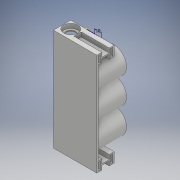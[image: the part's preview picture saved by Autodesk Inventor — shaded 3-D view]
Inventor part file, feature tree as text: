
AUTODESK INVENTOR PART (.ipt)
format: ipt  version: 2018 (Build 220112000, 112)  size: 634,368 bytes
history: native  units: mm
features: sketch x16, extrude x13, fillet x3
ambient origin geometry x8: Origin, YZ Plane, XZ Plane, XY Plane, X Axis, Y Axis, Z Axis, Center Point
bodies: Solid1 (feature_tree)
feature tree (32):
  extrude  "Extrusion1"  Depth=165.0mm
  extrude  "Extrusion2"  Depth=8.5mm
  extrude  "Extrusion3"  Depth=25.0mm TaperAngle=0.0deg
  extrude  "Extrusion4"  Depth=22.75mm
  extrude  "Extrusion5"  Depth=7.1mm
  extrude  "Extrusion6"  Depth=7.1mm TaperAngle=0.0deg
  fillet  "Fillet1"  Radius=5.0mm
  extrude  "Extrusion7"  Depth=10.0mm TaperAngle=0.0deg
  fillet  "Fillet2"  Radius=2.0mm
  extrude  "Extrusion8"  Depth=8.0mm
  extrude  "Extrusion9"  Depth=16.0mm
  fillet  "Fillet3"  Radius=8.0mm
  extrude  "Extrusion10"  Depth=6.0mm
  extrude  "Extrusion11"  Depth=3.5mm
  sketch  "Sketch12"  dims[d32=12.25mm d33=3.5mm]
  sketch  "Sketch13"  dims[d34=12.25mm d35=12.25mm]
  extrude  "Extrusion12"  Depth=3.5mm
  extrude  "Extrusion13"  Depth=12.25mm
  sketch  "Sketch16"  dims[d39=1.0mm d40=2.0mm d41=8.0mm d42=1.0mm d43=2.0mm d44=12.0mm d45=0.0mm d46=6.0mm d47=7.1mm d48=0.0mm d49=3.0mm d50=0.0mm d51=42.0mm d52=38.75mm d53=42.0mm d54=38.75mm d55=42.0mm d56=38.75mm d57=45.0mm d58=0.0mm d59=2.0mm d60=4.0mm d61=2.0mm d62=4.0mm d63=45.0mm d64=0.0mm d65=10.0mm]
  sketch  "Sketch1"  dims[d0=25.0mm d1=165.0mm]
  sketch  "Sketch2"  dims[d2=3.0mm d3=0.0mm d4=8.5mm]
  sketch  "Sketch3"  dims[d5=8.5mm d6=25.0mm d7=0.0mm]
  sketch  "Sketch4"  dims[d8=25.0mm d9=22.75mm]
  sketch  "Sketch5"  dims[d10=7.1mm d11=0.0mm d12=15.5mm]
  sketch  "Sketch6"  dims[d13=165.0mm d14=0.0mm d15=7.1mm d16=0.0mm d17=5.0mm]
  sketch  "Sketch7"  dims[d18=5.0mm d19=10.0mm d20=0.0mm d21=2.0mm]
  sketch  "Sketch8"  dims[d22=16.0mm d23=8.0mm]
  sketch  "Sketch9"  dims[d24=16.0mm d25=16.0mm d26=8.0mm]
  sketch  "Sketch10"  dims[d27=45.0mm d28=0.0mm d29=6.0mm]
  sketch  "Sketch11"  dims[d30=12.25mm d31=3.5mm]
  sketch  "Sketch14"  dims[d36=3.5mm]
  sketch  "Sketch15"  dims[d37=40.0mm d38=0.0mm]
